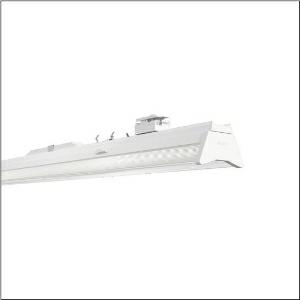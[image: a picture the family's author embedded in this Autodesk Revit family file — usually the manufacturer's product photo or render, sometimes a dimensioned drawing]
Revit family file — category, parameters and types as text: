
# Revit family: licross_r__11_performance_tw_51tm16tnt45x_2116
name_source: partatom
category: Lighting Fixtures
units: mm (PartAtom-declared; Revit-internal decimal feet)

## family parameters
Cut with Voids When Loaded = No
Host = Face
Light Source = No
Part Type = Normal
Room Calculation Point = No
Round Connector Dimension = Use Diameter
Shared = No

## types (1)
- --- (1 x LED 2700 K ... 6500 K, 4700 lm, 28.9 W, 2700K)
    Apparent Load = 29 VA
    CIE Flux Codes = 63 87 95 78 100
    Color Rendering = 80
    Color Temperature = 2700K
    Default Elevation = 1800 mm
    Description = Licross® 11 Performance TW, luminaire insert, of sheet steel, galvanised, coil coated, white, length: 1.500mm, width: 120mm, height: 123mm, LED rated luminous flux: 4.700lm, light colour: 8tw, control gear: DALI DT8, with plug, 5-pole, with phase selection, mains connection: 220..240V, AC, 50/60Hz, rated input power: 28.9W, internal wiring halogen-free, primary light control with lens, of plastic, primary optical cover: cover, of PMMA, light emission: direct/indirect distribution, primary light characteristic: symmetric, protection rating (complete): IP40, insulation class (complete): insulation class I (protective earthing), certification: CE, ENEC, VDE, UKCA, protection symbol: D if used in an environment without relevant dust loads with corresponding accessories, impact resistance: IK06, permissible ambient temperature for indoor applications: -25..+45°C, corresponds to IFS (International Featured Standards) requirements for safety and quality in the food industry, reducing of maximum allowable ambient temperature of 5°C with ceiling mounting, LABS conformity tested according to VDMA 24364:2018-05, packaging unit: 1 piece
    Height = 114 mm
    Lamp = 1 x LED 2700 K ... 6500 K
    Lamp Light Flux = 4700 lm
    Lamp Power = 28.9 W
    Lamp count = 1
    Length = 1500 mm
    Luminous efficacy = 163 lm/W
    Manufacturer = Siteco
    ModVariant = No
    Model = 51TM16TNT45X
    Mounting Place = Ceiling
    Mounting Type = Pendant
    Number of Poles = 1
    OnlyDefault = Yes
    Power Factor = 1
    Product Name = Licross® 11 Performance TW
    Product group = luminaire insert | ceiling pendant
    ProductGroupID = 902
    Protection Class = Protection class I
    Protection Degree = IP 40
    RLX_Detail_Level = 1
    RLX_Emergency_Light_Flux = 0 lm
    RLX_Emergency_Type = 0
    RLX_Emergency_Type_DB = No
    RlxData = <blob elided: 30393 chars, md5=d0502d8d>
    Socket = socket
    Standby Power = 0 W
    System Light Flux = 4700 lm
    System Power = 29 W
    Type Comments = individual setting: CCT=2700K
    Type Image = l_1256138.jpg
    URL = http://relux.com
    VarID = @adj_070085
    Voltage = 0 V
    Weight = 0.00 kg
    Width = 120 mm

## geometry (parser evidence)
native form markers: Blend x4, Sweep x13
no freeform markers — native parametric forms only
